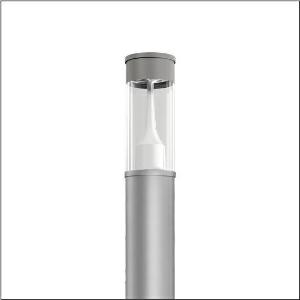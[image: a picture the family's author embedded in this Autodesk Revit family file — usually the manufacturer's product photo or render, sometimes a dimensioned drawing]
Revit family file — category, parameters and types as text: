
# Revit family: city-light_260_iq___pl1_2s_5xa5295cf14h_efd3
name_source: partatom
category: Lighting Fixtures
units: mm (PartAtom-declared; Revit-internal decimal feet)

## family parameters
Cut with Voids When Loaded = No
Host = Face
Light Source = No
Part Type = Normal
Room Calculation Point = No
Round Connector Dimension = Use Diameter
Shared = No

## types (1)
- --- (1 x LED, 2970 lm, 23.9 W, 2200K)
    Apparent Load = 24 VA
    CIE Flux Codes = 23 62 94 96 100
    Color Rendering = 70
    Color Temperature = 2200K
    Default Elevation = 1800 mm
    Description = City-Light 260 iQ, light pillar, Module 540 iQ-SR, primary light control with 3 zone facetted reflector, of plastic, silver coated, highly specular, structured, primary optical cover: cover, of PMMA, transparent, partly coated, light distribution: PL1.2s, primary light characteristic: symmetric, LED, High Power LED, rated luminous flux: 2.970lm, luminous efficacy: 124lm/W, light colour: 722, colour temperature: 2200K, control gear: iQ Street-Remote, control: pre-setting: logarithmic dimming characteristic, Street-Remote, Auto-Match, Temp-Guard, Lumen-Switch, Night-Set, Smart-Wire, Light-Fading, Desk-Remote (wireless, voltage-free reading and setting of iQ features in the workshop via application-optimized NFC function/RFID function), optimised constant luminous flux control (CLO 2.0), with terminal, 6-pole, max. 2.5mm², mains connection: 230..240V, AC, 50/60Hz, start of lifetime: 24W, end of service life: 26W, reduction: 12W, luminaire housing, cylindrical, of extruded aluminium section, coated, Siteco® metallic grey (DB 702S), length: 2.600mm, diameter: 200mm, Module 540 iQ-SR, traffic white (RAL 9016), equipment: standard, protection rating (complete): IP65, insulation class (complete): insulation class II (safety insulation), certification: CE, ENEC, VDE, packaging unit: 1 piece

Light Distribution: PL1.2s
    Height = 500 mm
    Lamp = 1 x LED
    Lamp Light Flux = 2970 lm
    Lamp Power = 23.9 W
    Lamp count = 1
    Length = 200 mm  [stored 0.656168 ft]
    Luminous efficacy = 124 lm/W
    Manufacturer = Siteco
    ModVariant = No
    Model = 5XA5295CF14H
    Mounting Place = Floor
    Mounting Type = Freestanding
    Number of Poles = 1
    OnlyDefault = Yes
    Power Factor = 1
    Product Name = City-Light 260 iQ | PL1.2s
    Product group = light pillar
    ProductGroupID = 1301
    Protection Class = Protection class II
    Protection Degree = IP 65
    RLX_Detail_Level = 1
    RLX_Emergency_Light_Flux = 0 lm
    RLX_Emergency_Type = 0
    RLX_Emergency_Type_DB = No
    RlxData = <blob elided: 28837 chars, md5=bbf78946>
    Socket = socket
    Standby Power = 0 W
    System Light Flux = 2970 lm
    System Power = 24 W
    Type Comments = factory setting: luminous flux: 100 % | dim-lin: 254 | 499 mA
    Type Image = l_1006920.jpg
    URL = http://relux.com
    VarID = @adj_146135
    Voltage = 0 V
    Weight = 0.00 kg
    Width = 0 mm  [stored 0 ft]

note: [stored X ft] marks values corroborated as IEEE doubles in the binary element streams (Revit-internal decimal feet)

## geometry (parser evidence)
native form markers: Blend x4, Sweep x11
no freeform markers — native parametric forms only
